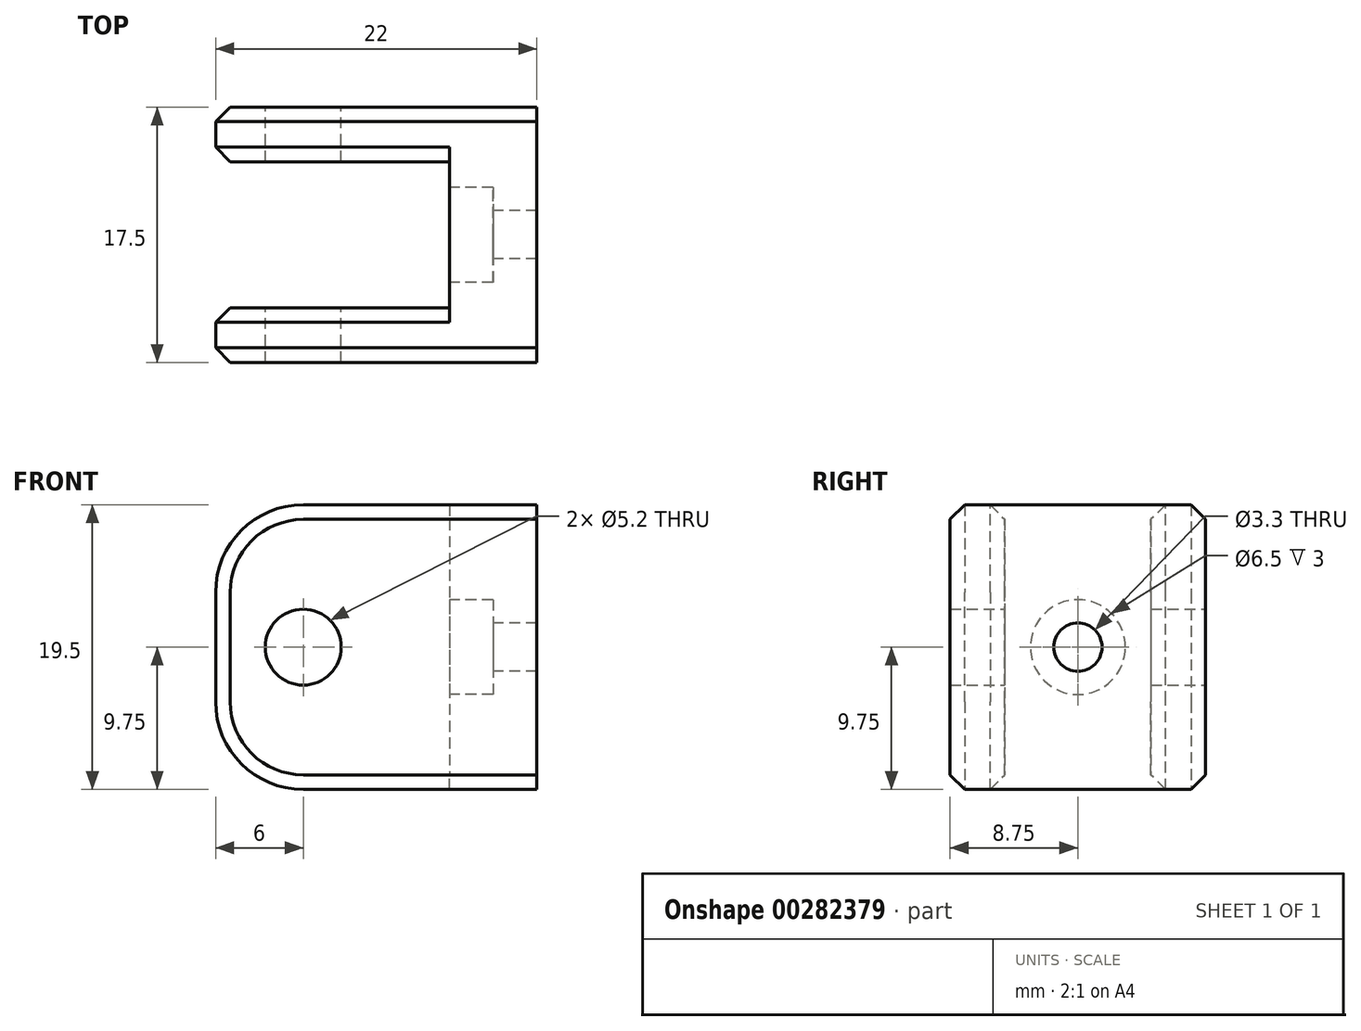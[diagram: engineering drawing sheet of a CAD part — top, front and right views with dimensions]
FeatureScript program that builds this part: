
annotation { "Feature Type Name" : "Feature", "Feature Type Description" : "" }
export const myFeature = defineFeature(function(context is Context, id is Id, definition is map)
    precondition{}
    {
        {
            var Q0;
            Q0=qCreatedBy(makeId("Top.planeOp"),FACE);
            var sketch = newSketch(context, id + "F0", { "sketchPlane" : qUnion([Q0])});
            skLineSegment(sketch, "E0.bottom", {"start": v(0, 0) * mm, "end": v(-22, 0) * mm});
            skLineSegment(sketch, "E0.top", {"start": v(0, 17.5) * mm, "end": v(-22, 17.5) * mm});
            skLineSegment(sketch, "E0.left", {"start": v(0, 0) * mm, "end": v(0, 17.5) * mm});
            skLineSegment(sketch, "E0.right", {"start": v(-22, 0) * mm, "end": v(-22, 3.75) * mm});
            skLineSegment(sketch, "E1.bottom", {"start": v(-22, 3.75) * mm, "end": v(-6, 3.75) * mm});
            skLineSegment(sketch, "E1.top", {"start": v(-22, 13.75) * mm, "end": v(-6, 13.75) * mm});
            skLineSegment(sketch, "E1.right", {"start": v(-6, 3.75) * mm, "end": v(-6, 13.75) * mm});
            skLineSegment(sketch, "E2.trimOffspring", {"start": v(-22, 13.75) * mm, "end": v(-22, 17.5) * mm});
            skLineSegment(sketch, "E3", {"start": v(-6, 8.75) * mm, "end": v(0, 8.75) * mm, "construction": true});
            skSolve(sketch);
        }
        {
            var Q0;
            Q0=qSketchRegion(id+"F0",true);
            extrude(context, id + "F1", {"entities" : qUnion([Q0]), "depth" : 19.5 * mm});
        }
        {
            var Q0;
            Q0=makeQuery(id+"F1.opExtrude","SWEPT_FACE",FACE,{"disambiguationData":[OSD([sQuery(id+"F0.wireOp",EDGE,"E0.top")])]});
            var sketch = newSketch(context, id + "F2", { "sketchPlane" : qUnion([Q0])});
            skLineSegment(sketch, "E4", {"start": v(0, 0) * mm, "end": v(0, 9.75) * mm, "construction": true});
            skLineSegment(sketch, "E5", {"start": v(0, 9.75) * mm, "end": v(16, 9.75) * mm, "construction": true});
            skCircle(sketch, "E6", {"center": v(16, 9.75) * mm, "radius": 2.6 * mm});
            skSolve(sketch);
        }
        {
            var Q0;
            Q0=qSketchRegion(id+"F2",true);
            extrude(context, id + "F3", {"entities" : qUnion([Q0]), "operationType" : NewBodyOperationType.REMOVE, "endBound" : BoundingType.THROUGH_ALL, "oppositeDirection" : true, "depth" : 25 * mm});
        }
        {
            var Q0;
            Q0=makeQuery(id+"F1.opExtrude","SWEPT_FACE",FACE,{"disambiguationData":[OSD([sQuery(id+"F0.wireOp",EDGE,"E1.right")])]});
            var sketch = newSketch(context, id + "F4", { "sketchPlane" : qUnion([Q0])});
            skLineSegment(sketch, "E7", {"start": v(-8.75, 19.5) * mm, "end": v(-8.75, 0) * mm, "construction": true});
            skPoint(sketch, "E8", {"position": v(-8.75, 9.75) * mm});
            skSolve(sketch);
        }
        {
            var Q0;
            Q0=sQuery(id+"F4.wireOp",VERTEX,"E8");
            var Q1;
            Q1=makeQuery(id+"F1.opExtrude","SWEPT_BODY",BODY,{"disambiguationData":[OSD([sQuery(id+"F0.wireOp",EDGE,"E0.bottom"),sQuery(id+"F0.wireOp",EDGE,"E0.top"),sQuery(id+"F0.wireOp",EDGE,"E0.left"),sQuery(id+"F0.wireOp",EDGE,"E0.right"),sQuery(id+"F0.wireOp",EDGE,"E1.bottom"),sQuery(id+"F0.wireOp",EDGE,"E1.top"),sQuery(id+"F0.wireOp",EDGE,"E1.right"),sQuery(id+"F0.wireOp",EDGE,"E2.trimOffspring")])]});
            hole(context, id + "F5", {"style" : HoleStyle.C_BORE, "endStyle" : HoleEndStyle.THROUGH, "standardTappedOrClearance" : lookupTablePath({ "standard" : "ISO", "fit" : "Normal", "size" : "M3", "type" : "Clearance" }), "standardBlindInLast" : lookupTablePath({ "fit" : "Standard", "standard" : "ISO", "size" : "M3", "type" : "Clearance" }), "holeDiameter" : 3.3 * mm, "cBoreDiameter" : 6.5 * mm, "cBoreDepth" : 3 * mm, "tappedDepth" : 3 * mm, "tapClearance" : 3, "startFromSketch" : true, "locations" : qUnion([Q0]), "scope" : qUnion([Q1])});
        }
        {
            var Q0;
            Q0=makeQuery(id+"F1.opExtrude","CAP_EDGE",EDGE,{"disambiguationData":[OSD([sQuery(id+"F0.wireOp",EDGE,"E2.trimOffspring")])],"isStart":true});
            var Q1;
            Q1=makeQuery(id+"F1.opExtrude","CAP_EDGE",EDGE,{"disambiguationData":[OSD([sQuery(id+"F0.wireOp",EDGE,"E2.trimOffspring")])],"isStart":false});
            var Q2;
            Q2=makeQuery(id+"F1.opExtrude","CAP_EDGE",EDGE,{"disambiguationData":[OSD([sQuery(id+"F0.wireOp",EDGE,"E0.right")])],"isStart":false});
            var Q3;
            Q3=makeQuery(id+"F1.opExtrude","CAP_EDGE",EDGE,{"disambiguationData":[OSD([sQuery(id+"F0.wireOp",EDGE,"E0.right")])],"isStart":true});
            fillet(context, id + "F6", {"entities" : qUnion([Q0, Q1, Q2, Q3]), "radius" : 6 * mm, "tangentPropagation" : true, "allowEdgeOverflow" : false});
        }
        {
            var Q0;
            Q0=makeQuery(id+"F1.opExtrude","CAP_EDGE",EDGE,{"disambiguationData":[OSD([sQuery(id+"F0.wireOp",EDGE,"E0.top")])],"isStart":true});
            var Q1;
            Q1=makeQuery(id+"F1.opExtrude","CAP_EDGE",EDGE,{"disambiguationData":[OSD([sQuery(id+"F0.wireOp",EDGE,"E0.bottom")])],"isStart":true});
            var Q2;
            Q2=makeQuery(id+"F1.opExtrude","CAP_EDGE",EDGE,{"disambiguationData":[OSD([sQuery(id+"F0.wireOp",EDGE,"E1.bottom")])],"isStart":true});
            var Q3;
            Q3=makeQuery(id+"F1.opExtrude","CAP_EDGE",EDGE,{"disambiguationData":[OSD([sQuery(id+"F0.wireOp",EDGE,"E1.top")])],"isStart":true});
            chamfer(context, id + "F7", {"entities" : qUnion([Q0, Q1, Q2, Q3]), "width" : 1 * mm, "tangentPropagation" : true});
        }
    });
